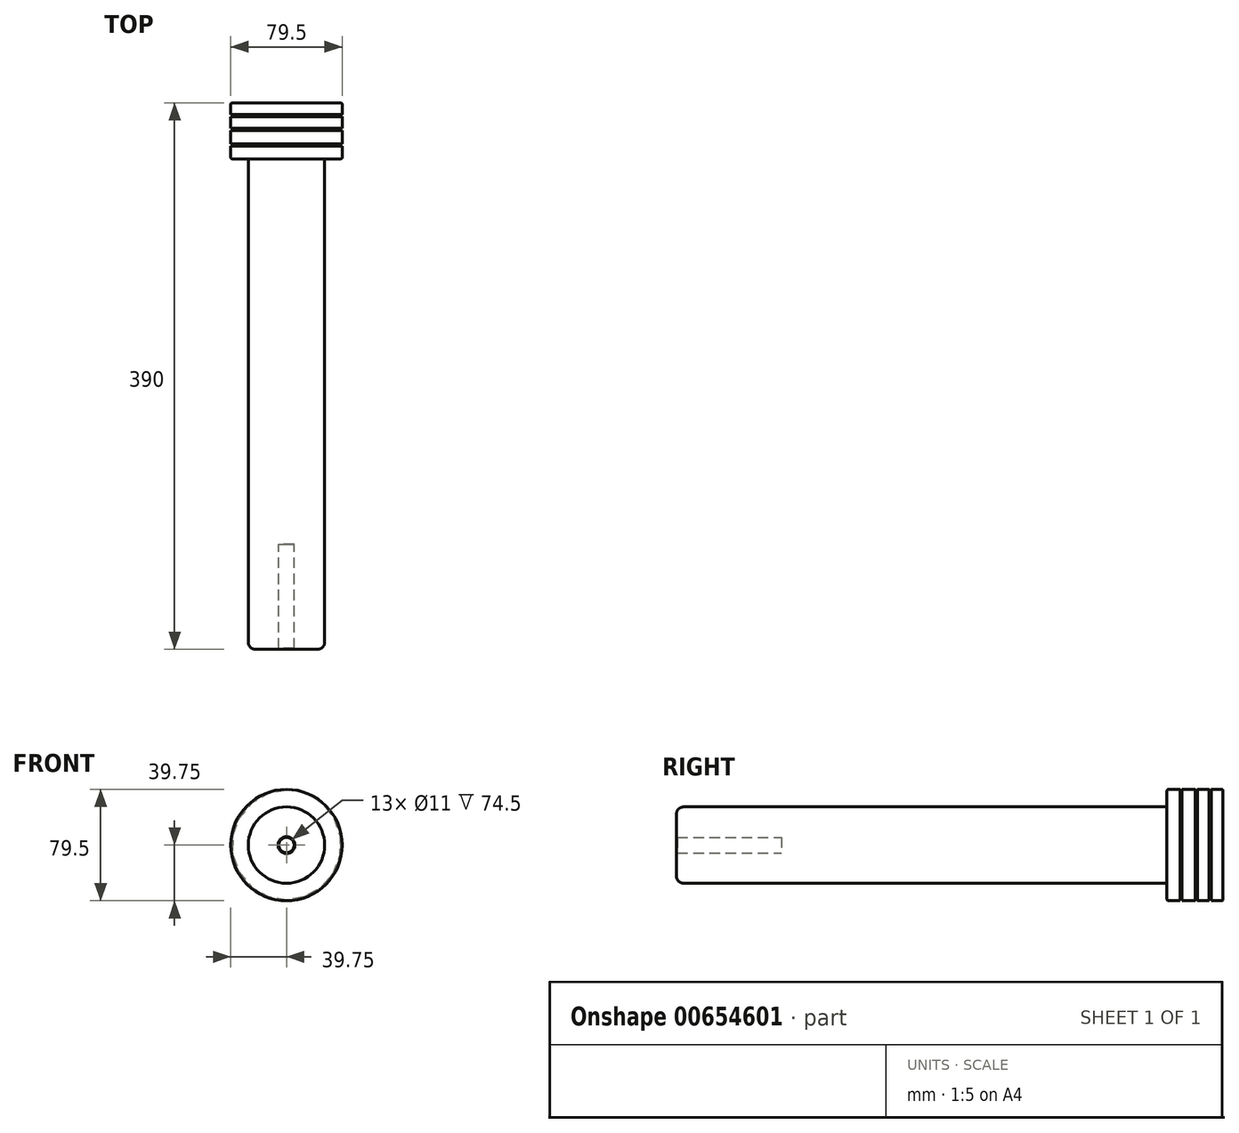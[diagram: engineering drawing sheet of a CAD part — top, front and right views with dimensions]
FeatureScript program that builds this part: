
annotation { "Feature Type Name" : "Feature", "Feature Type Description" : "" }
export const myFeature = defineFeature(function(context is Context, id is Id, definition is map)
    precondition{}
    {
        {
            var Q0;
            Q0=qCreatedBy(makeId("Top.planeOp"),FACE);
            var sketch = newSketch(context, id + "F0", { "sketchPlane" : qUnion([Q0])});
            skLineSegment(sketch, "E0", {"start": v(0, 148.8) * mm, "end": v(0, -166.2) * mm});
            skLineSegment(sketch, "E1", {"start": v(0, 148.8) * mm, "end": v(-38.75, 148.8) * mm});
            skLineSegment(sketch, "E2", {"start": v(-39.75, 147.8) * mm, "end": v(-39.75, 140.45) * mm});
            skLineSegment(sketch, "E3", {"start": v(-39.75, 138.95) * mm, "end": v(-39.75, 130.45) * mm});
            skLineSegment(sketch, "E4", {"start": v(-39.75, 128.95) * mm, "end": v(-39.75, 119.54) * mm});
            skLineSegment(sketch, "E5", {"start": v(-27.25, 105.8) * mm, "end": v(-27.25, -236.2) * mm});
            skLineSegment(sketch, "E6", {"start": v(-5.5, -241.2) * mm, "end": v(-22.25, -241.2) * mm});
            skArc(sketch, "E7", {"start": v(-39.75, 138.95) * mm, "mid": v(-39, 139.7) * mm, "end": v(-39.75, 140.45) * mm});
            skLineSegment(sketch, "E8", {"start": v(-39.75, 118.04) * mm, "end": v(-39.75, 109.8) * mm});
            skLineSegment(sketch, "E9", {"start": v(-38.75, 108.8) * mm, "end": v(-30.25, 108.8) * mm});
            skArc(sketch, "E10", {"start": v(-39.75, 118.04) * mm, "mid": v(-39, 118.8) * mm, "end": v(-39.75, 119.54) * mm});
            skLineSegment(sketch, "E11.bottom", {"start": v(-39, 130.45) * mm, "end": v(-39.75, 130.45) * mm});
            skLineSegment(sketch, "E11.top", {"start": v(-39, 128.95) * mm, "end": v(-39.75, 128.95) * mm});
            skLineSegment(sketch, "E11.left", {"start": v(-39, 130.45) * mm, "end": v(-39, 128.95) * mm});
            skPoint(sketch, "E11.middle", {"position": v(-39.75, 129.7) * mm});
            skPoint(sketch, "E12.orphan", {"position": v(-40.5, 128.95) * mm});
            skPoint(sketch, "E13.orphan", {"position": v(-40.5, 130.45) * mm});
            skPoint(sketch, "E14.visualSharp", {"position": v(-27.25, 108.8) * mm});
            skPoint(sketch, "E15.visualSharp", {"position": v(-39.75, 148.8) * mm});
            skArc(sketch, "E15.filletArc", {"start": v(-38.75, 148.8) * mm, "mid": v(-39.46, 148.5) * mm, "end": v(-39.75, 147.8) * mm});
            skPoint(sketch, "E16.visualSharp", {"position": v(-39.75, 108.8) * mm});
            skArc(sketch, "E16.filletArc", {"start": v(-39.75, 109.8) * mm, "mid": v(-39.46, 109.09) * mm, "end": v(-38.75, 108.8) * mm});
            skPoint(sketch, "E17.visualSharp", {"position": v(-27.25, -241.2) * mm});
            skArc(sketch, "E17.filletArc", {"start": v(-27.25, -236.2) * mm, "mid": v(-25.79, -239.74) * mm, "end": v(-22.25, -241.2) * mm});
            skLineSegment(sketch, "E18", {"start": v(0, -166.2) * mm, "end": v(-5.5, -166.2) * mm});
            skLineSegment(sketch, "E19", {"start": v(-5.5, -166.2) * mm, "end": v(-5.5, -241.2) * mm});
            skPoint(sketch, "E20.orphan", {"position": v(0, -241.2) * mm});
            skLineSegment(sketch, "E21", {"start": v(-27.25, 105.8) * mm, "end": v(-27.25, 108.8) * mm});
            skLineSegment(sketch, "E22", {"start": v(-27.25, 108.8) * mm, "end": v(-30.25, 108.8) * mm});
            skSolve(sketch);
        }
        {
            var Q0;
            Q0=makeQuery(id+"F0.imprint","IMPRINT",FACE,{"disambiguationData":[TD([[makeQuery(id+"F0.imprint","IMPRINT",EDGE,{"derivedFrom":sQuery(id+"F0.wireOp",EDGE,"E0")}),-1.0]])]});
            var Q1;
            Q1=sQuery(id+"F0.wireOp",EDGE,"E0");
            revolve(context, id + "F1", {"entities" : qUnion([Q0]), "axis" : qUnion([Q1]), "revolveType" : RevolveType.FULL});
        }
        {
            var Q0;
            Q0=makeQuery(id+"F1.opRevolve","SWEPT_FACE",FACE,{"disambiguationData":[OSD([sQuery(id+"F0.wireOp",EDGE,"E6")])]});
            chamfer(context, id + "F2", {"entities" : qUnion([Q0]), "width" : 0.5 * mm, "tangentPropagation" : true});
        }
    });
